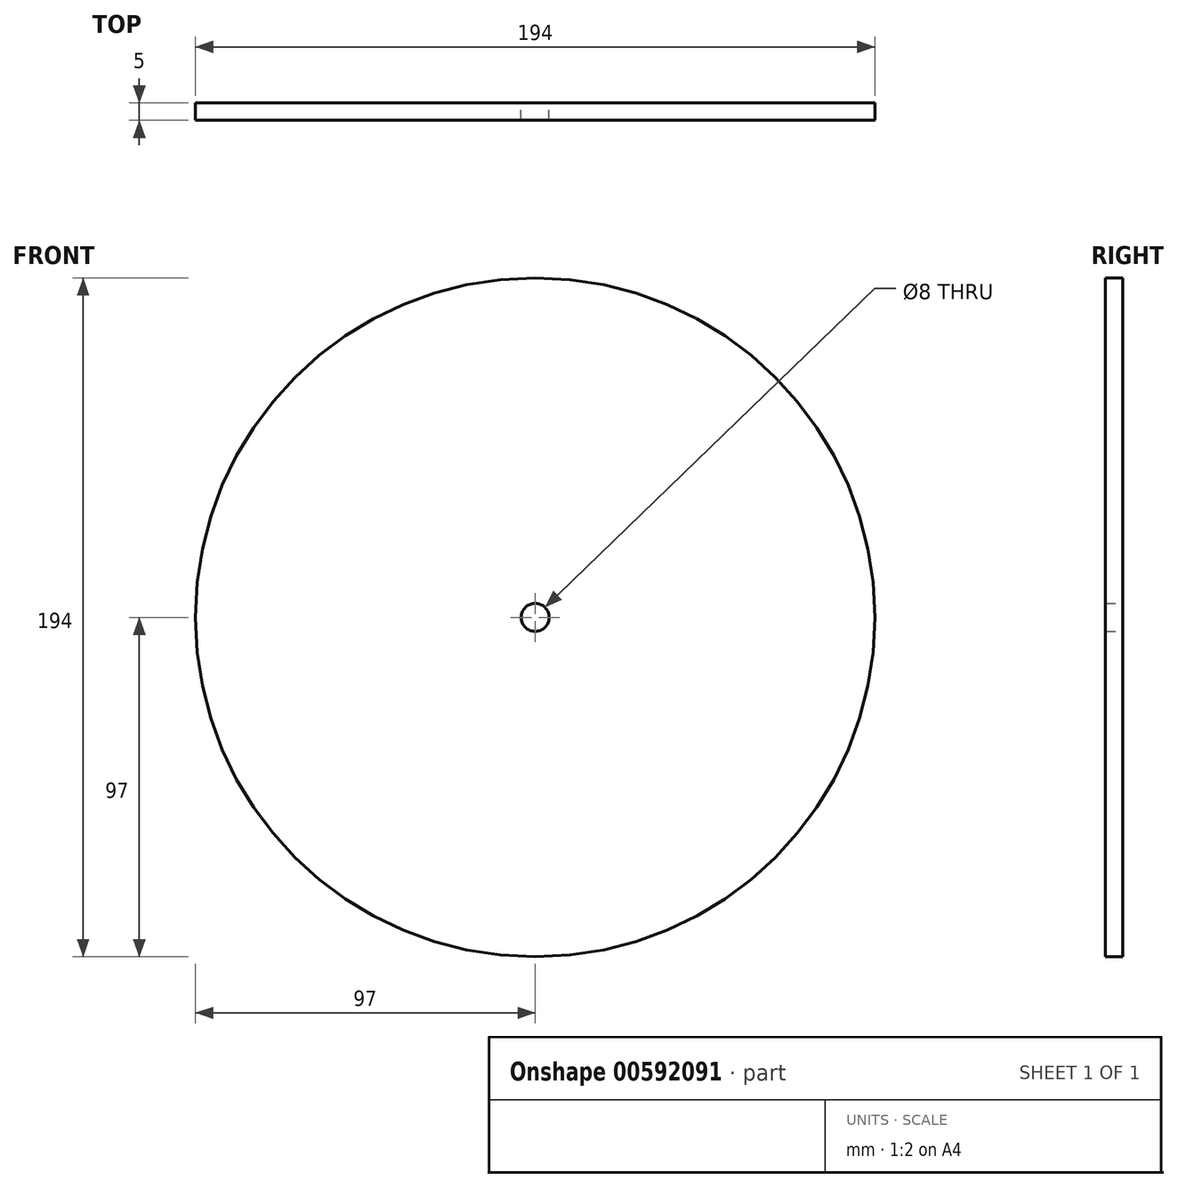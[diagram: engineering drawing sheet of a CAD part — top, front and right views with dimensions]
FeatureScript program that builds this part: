
annotation { "Feature Type Name" : "Feature", "Feature Type Description" : "" }
export const myFeature = defineFeature(function(context is Context, id is Id, definition is map)
    precondition{}
    {
        {
            var Q0;
            Q0=qCreatedBy(makeId("Front.planeOp"),FACE);
            var sketch = newSketch(context, id + "F0", { "sketchPlane" : qUnion([Q0])});
            skCircle(sketch, "E0", {"center": v(0, 0) * mm, "radius": 97 * mm});
            skCircle(sketch, "E1", {"center": v(0, 0) * mm, "radius": 4 * mm});
            skSolve(sketch);
        }
        {
            var Q0;
            Q0=makeQuery(id+"F0.imprint","IMPRINT",FACE,{"disambiguationData":[TD([[makeQuery(id+"F0.imprint","IMPRINT",EDGE,{"derivedFrom":sQuery(id+"F0.wireOp",EDGE,"E0")}),1.0]])]});
            extrude(context, id + "F1", {"entities" : qUnion([Q0]), "depth" : 5 * mm, "offsetDistance" : 25.4 * mm});
        }
    });
